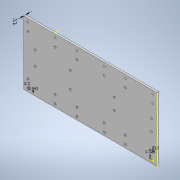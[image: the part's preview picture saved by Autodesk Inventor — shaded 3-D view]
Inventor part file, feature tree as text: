
AUTODESK INVENTOR PART (.ipt)
format: ipt  version: 2020 (Build 240168000, 168)  size: 276,480 bytes
history: native  units: in
note: dims shown in document units (in); Inventor stores cm internally (conversion verified against a paired STEP export)
features: sketch x34, hole x32, other x2, extrude x1
ambient origin geometry x8: Origin, YZ Plane, XZ Plane, XY Plane, X Axis, Y Axis, Z Axis, Center Point
bodies: Solid1 (feature_tree)
feature tree (69):
  other  "Annotations"
  sketch  "Sketch1"  dims[d3=0.12in d4=0.0in]
  extrude  "Extrusion1"  Depth=0.2756in
  hole  "Hole1"  [1 undecoded]
  hole  "Hole2"  [1 undecoded]
  hole  "Hole3"  [1 undecoded]
  hole  "Hole4"  [1 undecoded]
  hole  "Hole5"  [1 undecoded]
  hole  "Hole6"  [1 undecoded]
  hole  "Hole7"  [1 undecoded]
  hole  "Hole8"  [1 undecoded]
  hole  "Hole9"  [1 undecoded]
  hole  "Hole10"  [1 undecoded]
  hole  "Hole11"  [1 undecoded]
  hole  "Hole12"  [1 undecoded]
  hole  "Hole14"  [1 undecoded]
  hole  "Hole15"  [1 undecoded]
  hole  "Hole13"  [1 undecoded]
  hole  "Hole16"  [1 undecoded]
  hole  "Hole17"  [1 undecoded]
  hole  "Hole18"  [1 undecoded]
  hole  "Hole19"  [1 undecoded]
  hole  "Hole20"  [1 undecoded]
  hole  "Hole21"  [1 undecoded]
  hole  "Hole22"  [1 undecoded]
  hole  "Hole23"  [1 undecoded]
  hole  "Hole24"  [1 undecoded]
  hole  "Hole25"  [1 undecoded]
  hole  "Hole26"  [1 undecoded]
  hole  "Hole27"  [1 undecoded]
  hole  "Hole28"  [1 undecoded]
  hole  "Hole29"  [1 undecoded]
  hole  "Hole30"  [1 undecoded]
  hole  "Hole31"  [1 undecoded]
  hole  "Hole32"  [1 undecoded]
  sketch  "Sketch2"  dims[d5=0.114in d6=0.75in d7=0.375in d8=0.25in d9=0.5635in d10=1.0in d11=0.8108in d18=0.2756in]
  sketch  "Sketch3"  dims[d19=0.213in]
  sketch  "Sketch6"  dims[d22=0.114in d23=0.75in d24=0.375in d25=0.25in d26=0.5635in d27=1.0in d28=0.8108in d31=0.2756in]
  sketch  "Sketch7"  dims[d32=0.522in]
  sketch  "Sketch8"  dims[d33=0.114in d34=0.75in d35=0.375in d36=0.25in d37=0.5635in d38=1.0in d39=0.8108in d40=1.77in]
  sketch  "Sketch10"  dims[d41=0.213in]
  sketch  "Sketch11"  dims[d42=0.114in d43=0.75in d44=0.375in d45=0.25in d46=0.5635in d47=1.0in d48=0.8108in d50=1.77in]
  sketch  "Sketch12"  dims[d51=0.522in]
  sketch  "Sketch13"  dims[d52=0.114in d53=0.75in d54=0.375in d55=0.25in d56=0.5635in d57=1.0in d58=0.8108in d59=0.21in]
  sketch  "Sketch14"  dims[d60=0.2756in]
  sketch  "Sketch15"  dims[d61=0.114in d62=0.75in d63=0.375in d64=0.25in d65=0.5635in d66=1.0in d67=0.8108in d68=0.2756in]
  sketch  "Sketch16"  dims[d70=0.522in]
  sketch  "Sketch17"  dims[d71=0.114in d72=0.75in d73=0.375in d74=0.25in d75=0.5635in d76=1.0in d77=0.8108in d78=0.213in]
  sketch  "Sketch18"  dims[d79=1.77in]
  sketch  "Sketch19"  dims[d80=0.114in d81=0.75in d82=0.375in d83=0.25in d84=0.5635in d85=1.0in d86=0.8108in d87=0.522in]
  sketch  "Sketch20"  dims[d88=1.772in]
  sketch  "Sketch21"  dims[d89=0.114in d90=0.75in d91=0.375in d92=0.25in d93=0.5635in d94=1.0in d95=0.8108in d96=0.213in]
  sketch  "Sketch22"  dims[d97=0.2756in]
  sketch  "Sketch23"  dims[d98=0.114in d99=0.75in d100=0.375in d101=0.25in d102=0.5635in d103=1.0in d104=0.8108in d105=0.213in]
  sketch  "Sketch24"  dims[d106=0.2756in]
  sketch  "Sketch25"  dims[d107=0.114in d108=0.75in d109=0.375in d110=0.25in d111=0.5635in d112=1.0in d113=0.8108in d114=0.213in]
  sketch  "Sketch26"  dims[d115=1.77in]
  sketch  "Sketch27"  dims[d116=0.114in d117=0.75in d118=0.375in d119=0.25in d120=0.5635in d121=1.0in d122=0.8108in d123=0.213in]
  sketch  "Sketch28"  dims[d124=1.77in]
  sketch  "Sketch29"  dims[d125=0.114in d126=0.75in d127=0.375in d128=0.25in d129=0.5635in d130=1.0in d131=0.8108in]
  sketch  "Sketch30"  dims[d132=0.114in d133=0.75in d134=0.375in d135=0.25in d136=0.5635in d137=1.0in d138=0.8108in]
  sketch  "Sketch31"  dims[d139=0.114in d140=0.75in d141=0.375in d142=0.25in d143=0.5635in d144=1.0in d145=0.8108in d146=0.2756in]
  sketch  "Sketch32"  dims[d147=0.522in d148=0.522in]
  sketch  "Sketch33"  dims[d149=1.775in d150=0.522in]
  sketch  "Sketch34"  dims[d151=0.2756in]
  sketch  "Sketch35"  dims[d152=0.114in d153=0.75in d154=0.375in d155=0.25in d156=0.5635in d157=1.0in d158=0.8108in d159=1.77in]
  sketch  "Sketch36"  dims[d160=0.522in]
  sketch  "Sketch37"  dims[d161=0.114in d162=0.75in d163=0.375in d164=0.25in d165=0.5635in d166=1.0in d167=0.8108in d168=0.213in d169=0.114in d170=0.75in d171=0.375in d172=0.25in d173=0.5635in d174=1.0in d175=0.8108in d176=0.213in d177=1.77in d178=1.378in d179=0.114in d180=0.75in d181=0.375in d182=0.25in d183=0.5635in d184=1.0in d185=0.8108in d186=0.114in d187=0.75in d188=0.375in d189=0.25in d190=0.5635in d191=1.0in d192=0.8108in d193=1.378in d194=0.522in d195=0.522in d196=1.77in d197=0.114in d198=0.75in d199=0.375in d200=0.25in d201=0.5635in d202=1.0in d203=0.8108in d204=0.114in d205=0.75in d206=0.375in d207=0.25in d208=0.5635in d209=1.0in d210=0.8108in d211=0.114in d212=0.75in d213=0.375in d214=0.25in d215=0.5635in d216=1.0in d217=0.8108in d218=0.114in d219=0.75in d220=0.375in d221=0.25in d222=0.5635in d223=1.0in d224=0.8108in d225=1.378in d226=0.213in d227=0.213in d228=1.77in d229=0.52in d230=1.378in d231=1.77in d232=0.522in d235=0.114in d236=0.75in d237=0.375in d238=0.25in d239=0.5635in d240=1.0in d241=0.8108in d242=0.75in d243=0.114in d244=0.75in d245=0.375in d246=0.25in d247=0.5635in d248=1.0in d249=0.8108in d250=0.75in d251=0.937in d256=1.535in d257=0.114in d258=0.75in d259=0.375in d260=0.25in d261=0.5635in d262=1.0in d263=0.8108in d264=2.279in d265=1.54in d266=0.114in d267=0.75in d268=0.375in d269=0.25in d270=0.5635in d271=1.0in d272=0.8108in d273=2.279in d274=1.53in d275=0.114in d276=0.75in d277=0.375in d278=0.25in d279=0.5635in d280=1.0in d281=0.8108in d282=0.35in d283=0.114in d284=0.75in d285=0.375in d286=0.25in d287=0.5635in d288=1.0in d289=0.8108in d290=0.35in d295=1.625in d296=0.746in d297=0.114in d298=0.75in d299=0.375in d300=0.25in d301=0.5635in d302=1.0in d303=0.8108in d304=2.41in d305=1.63in d306=0.114in d307=0.75in d308=0.375in d309=0.25in d310=0.5635in d311=1.0in d312=0.8108in d313=0.746in d314=2.417in d316=8.6614in d12=0.35in d13=0.12in]
  other  "Linear Dimension 1"
note: 32 required parameter values undecoded (feature->parameter linkage not recoverable at this tier; creation-order binding heuristic only, values carry confidence <= 0.55)
